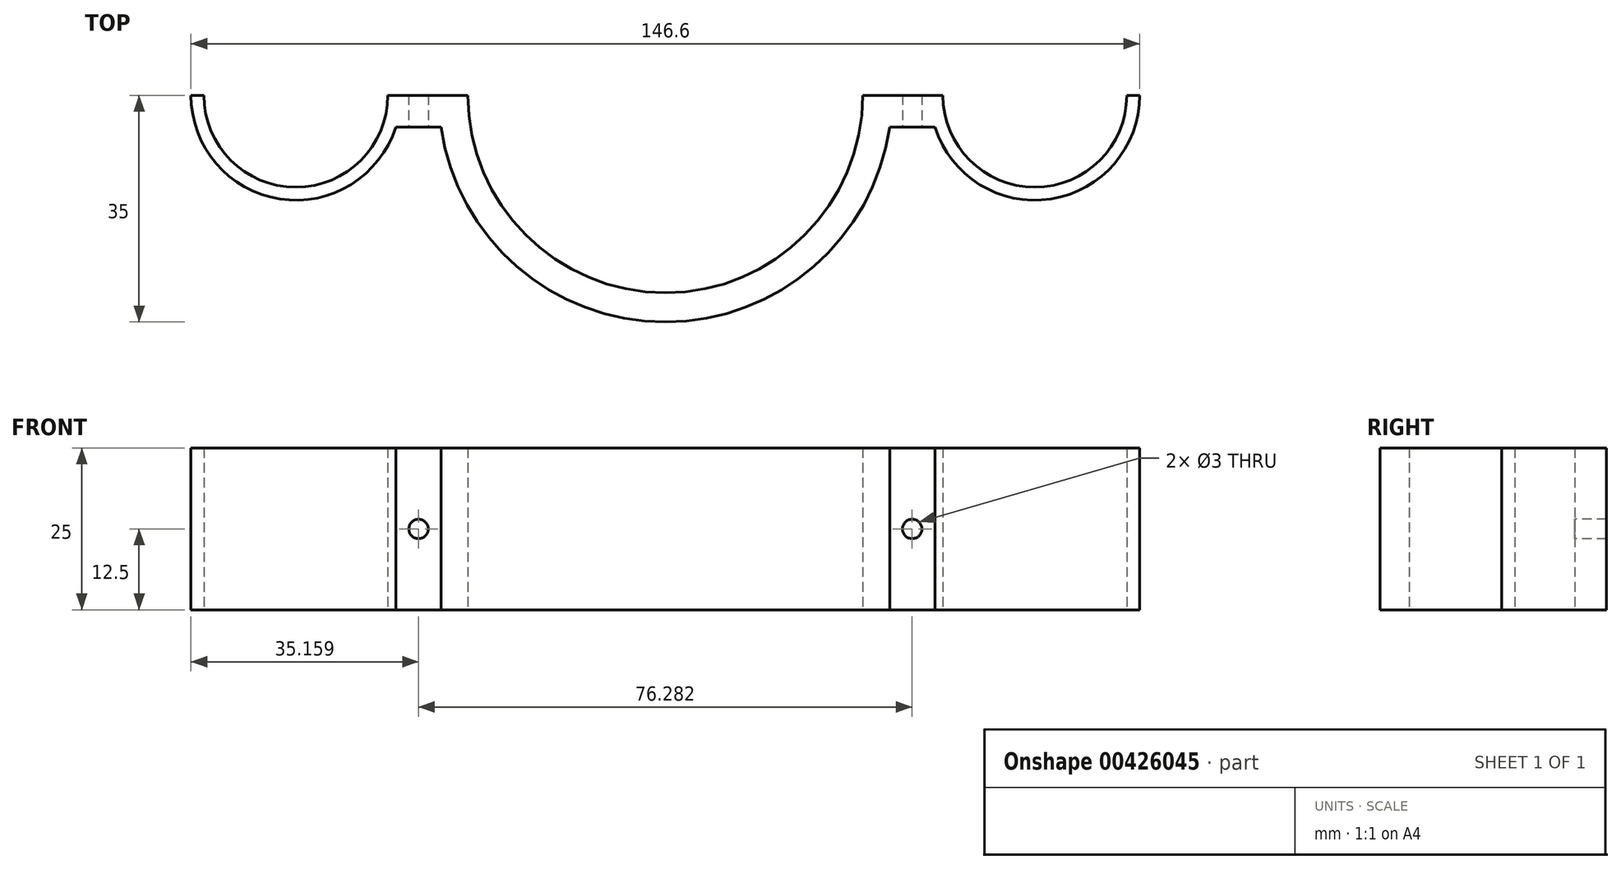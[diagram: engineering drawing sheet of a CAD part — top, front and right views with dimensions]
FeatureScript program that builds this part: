
annotation { "Feature Type Name" : "Feature", "Feature Type Description" : "" }
export const myFeature = defineFeature(function(context is Context, id is Id, definition is map)
    precondition{}
    {
        {
            var Q0;
            Q0=qCreatedBy(makeId("Top.planeOp"),FACE);
            var sketch = newSketch(context, id + "F0", { "sketchPlane" : qUnion([Q0])});
            skArc(sketch, "E0", {"start": v(-30.5, 0) * mm, "mid": v(0, -30.5) * mm, "end": v(30.5, 0) * mm});
            skArc(sketch, "E1", {"start": v(-34.66, -4.89) * mm, "mid": v(0.45, -35) * mm, "end": v(34.77, -4) * mm});
            skLineSegment(sketch, "E2", {"start": v(30.5, 0) * mm, "end": v(35, 0) * mm, "construction": true});
            skLineSegment(sketch, "E3", {"start": v(-35, 0) * mm, "end": v(-30.5, 0) * mm, "construction": true});
            skLineSegment(sketch, "E4.bottom", {"start": v(-30.5, 0) * mm, "end": v(-35, 0) * mm});
            skLineSegment(sketch, "E4.top", {"start": v(-42.8, 0) * mm, "end": v(-42.8, 0) * mm});
            skLineSegment(sketch, "E4.right", {"start": v(-42.8, 0) * mm, "end": v(-42.8, 0) * mm});
            skLineSegment(sketch, "E5.MirrorCS", {"start": v(42.8, 0) * mm, "end": v(42.8, 0) * mm});
            skLineSegment(sketch, "E6.MirrorCS", {"start": v(30.5, 0) * mm, "end": v(35, 0) * mm});
            skPoint(sketch, "E7.centerSnap0", {"position": v(-42.8, 0) * mm});
            skPoint(sketch, "E8.orphan", {"position": v(-61.93, 0) * mm});
            skPoint(sketch, "E9.end.orphan", {"position": v(-61.93, -2) * mm});
            skPoint(sketch, "E10.start.orphan", {"position": v(42.8, -5.25) * mm});
            skPoint(sketch, "E11.orphan", {"position": v(42.8, 0) * mm});
            skPoint(sketch, "E12.orphan", {"position": v(-35, 0) * mm});
            skPoint(sketch, "E13.end.orphan", {"position": v(-58.21, 0) * mm});
            skPoint(sketch, "E14.start.orphan", {"position": v(-64.8, 0) * mm});
            skPoint(sketch, "E15.start.orphan", {"position": v(-43.91, 0) * mm});
            skArc(sketch, "E16", {"start": v(-71.3, 0) * mm, "mid": v(-57.1, -14.2) * mm, "end": v(-42.9, 0) * mm});
            skPoint(sketch, "E17.MirrorCS.start.orphan", {"position": v(64.8, 0) * mm});
            skPoint(sketch, "E18.MirrorCS.end.orphan", {"position": v(43.91, 0) * mm});
            skPoint(sketch, "E18.MirrorCS.start.orphan", {"position": v(58.21, 0) * mm});
            skPoint(sketch, "E19.MirrorCS.end.orphan", {"position": v(61.93, 0) * mm});
            skPoint(sketch, "E20.MirrorCS.start.orphan", {"position": v(35, 0) * mm});
            skArc(sketch, "E21.trimOffspring", {"start": v(-73.3, 0) * mm, "mid": v(-59.58, -16.01) * mm, "end": v(-41.66, -4.89) * mm});
            skPoint(sketch, "E22.end.orphan", {"position": v(-35, -4.89) * mm});
            skLineSegment(sketch, "E23", {"start": v(-41.66, -4.89) * mm, "end": v(-34.66, -4.89) * mm});
            skLineSegment(sketch, "E24.MirrorCS", {"start": v(41.66, -4.89) * mm, "end": v(34.66, -4.89) * mm});
            skLineSegment(sketch, "E25.MirrorCS", {"start": v(30.5, 0) * mm, "end": v(40.9, 0) * mm});
            skArc(sketch, "E26.MirrorCS", {"start": v(73.3, 0) * mm, "mid": v(59.58, -16.01) * mm, "end": v(41.66, -4.89) * mm});
            skArc(sketch, "E27.MirrorCS", {"start": v(71.3, 0) * mm, "mid": v(57.1, -14.2) * mm, "end": v(42.9, 0) * mm});
            skPoint(sketch, "E28.MirrorP", {"position": v(35, -4.89) * mm});
            skLineSegment(sketch, "E29", {"start": v(-71.3, 0) * mm, "end": v(-73.3, 0) * mm});
            skPoint(sketch, "E30.MirrorCS.start.orphan", {"position": v(-72.09, 6.15) * mm});
            skPoint(sketch, "E31.orphan", {"position": v(-70.46, 4.83) * mm});
            skPoint(sketch, "E32.start.orphan", {"position": v(-42.11, 6.15) * mm});
            skPoint(sketch, "E33.orphan", {"position": v(-40.9, 0) * mm});
            skLineSegment(sketch, "E34", {"start": v(-35, 0) * mm, "end": v(-42.9, 0) * mm});
            skLineSegment(sketch, "E35", {"start": v(-42.9, 0) * mm, "end": v(-42.8, 0) * mm});
            skPoint(sketch, "E36.orphan", {"position": v(-43.75, 4.83) * mm});
            skLineSegment(sketch, "E37.MirrorCS", {"start": v(71.3, 0) * mm, "end": v(73.3, 0) * mm});
            skLineSegment(sketch, "E38.MirrorCS", {"start": v(35, 0) * mm, "end": v(42.9, 0) * mm});
            skPoint(sketch, "E39.MirrorCS.end.orphan", {"position": v(43.75, 4.83) * mm});
            skPoint(sketch, "E39.MirrorCS.start.orphan", {"position": v(42.11, 6.15) * mm});
            skPoint(sketch, "E40.MirrorCS.start.orphan", {"position": v(40.9, 0) * mm});
            skPoint(sketch, "E41.orphan", {"position": v(70.46, 4.83) * mm});
            skPoint(sketch, "E42.MirrorCS.start.orphan", {"position": v(72.09, 6.15) * mm});
            skSolve(sketch);
        }
        {
            var Q0;
            {var subQ1=sQuery(id+"F0.wireOp",EDGE,"E0");Q0=makeQuery(id+"F0.imprint","IMPRINT",FACE,{"disambiguationData":[TD([[makeQuery(id+"F0.imprint","IMPRINT",EDGE,{"derivedFrom":subQ1}),-1.0]])]});}
            extrude(context, id + "F1", {"entities" : qUnion([Q0]), "depth" : 25 * mm, "offsetDistance" : 25 * mm});
        }
        {
            var Q0;
            Q0=makeQuery(id+"F1.opExtrude","SWEPT_FACE",FACE,{"disambiguationData":[OSD([sQuery(id+"F0.wireOp",EDGE,"E23")])]});
            var sketch = newSketch(context, id + "F2", { "sketchPlane" : qUnion([Q0])});
            skLineSegment(sketch, "E43", {"start": v(-41.66, 12.5) * mm, "end": v(41.8, 12.5) * mm, "construction": true});
            skPoint(sketch, "E44.end.orphan", {"position": v(38.14, 0) * mm});
            skLineSegment(sketch, "E45", {"start": v(38.14, 0) * mm, "end": v(38.14, 25.03) * mm, "construction": true});
            skCircle(sketch, "E46", {"center": v(38.14, 12.5) * mm, "radius": 1.5 * mm});
            skPoint(sketch, "E46.centerSnap0", {"position": v(38.14, 12.51) * mm});
            skCircle(sketch, "E47.MirrorC", {"center": v(-38.14, 12.5) * mm, "radius": 1.5 * mm});
            skSolve(sketch);
        }
        {
            var Q0;
            Q0 = qSketchRegion(id + "F2", true);
            extrude(context, id + "F3", {"entities" : qUnion([Q0]), "operationType" : NewBodyOperationType.REMOVE, "oppositeDirection" : true, "depth" : 25 * mm, "offsetDistance" : 25 * mm});
        }
    });
